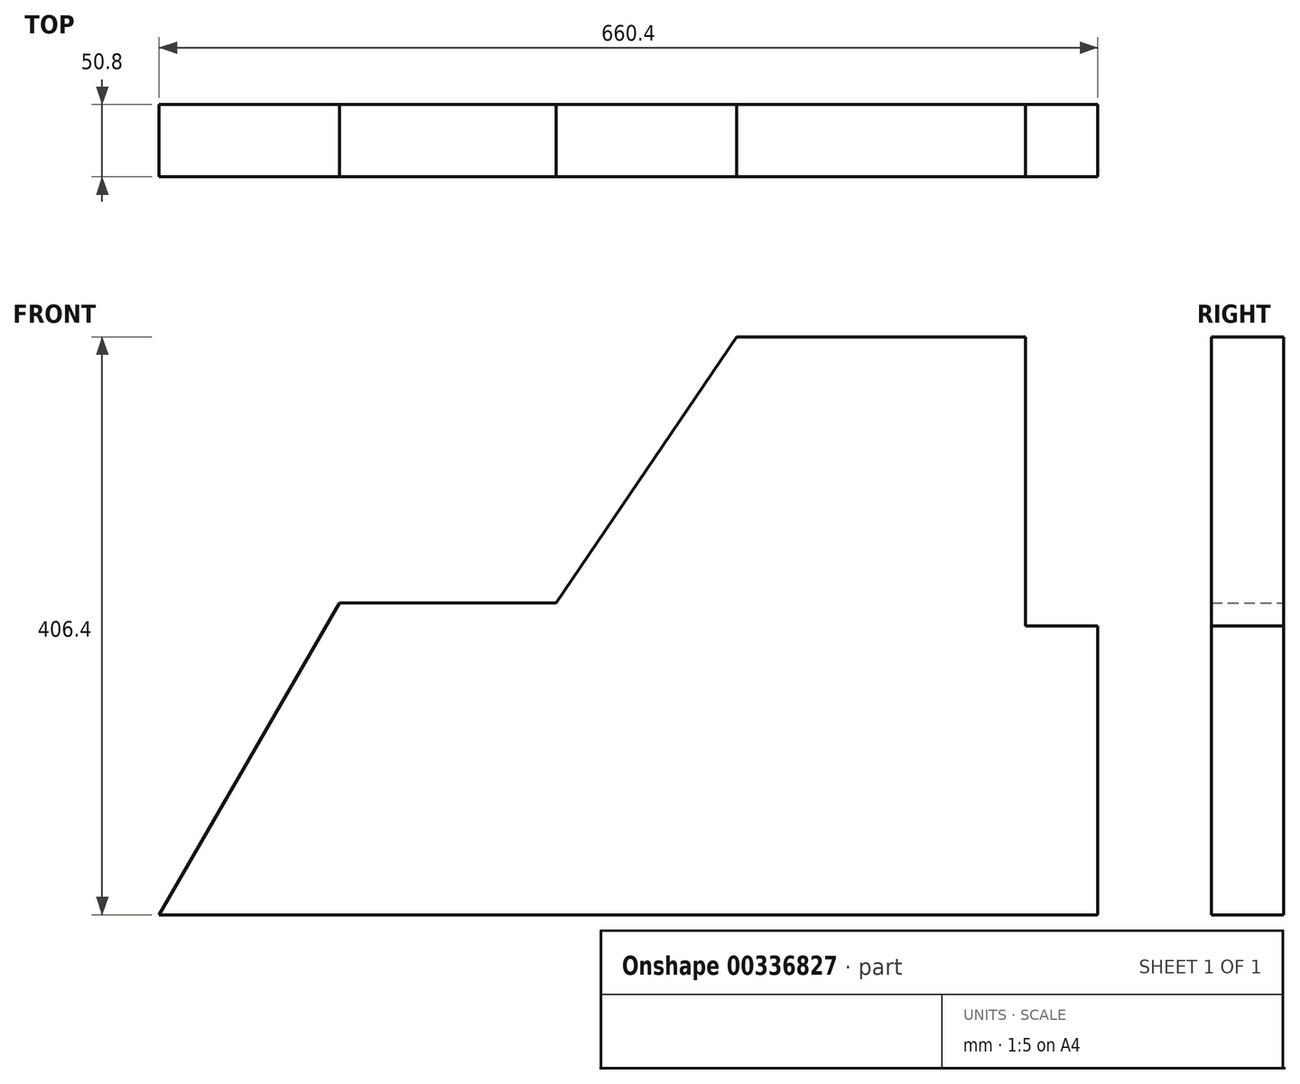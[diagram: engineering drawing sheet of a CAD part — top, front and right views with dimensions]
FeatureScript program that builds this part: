
annotation { "Feature Type Name" : "Feature", "Feature Type Description" : "" }
export const myFeature = defineFeature(function(context is Context, id is Id, definition is map)
    precondition{}
    {
        {
            var Q0;
            Q0=qCreatedBy(makeId("Front.planeOp"),FACE);
            var sketch = newSketch(context, id + "F0", { "sketchPlane" : qUnion([Q0])});
            skLineSegment(sketch, "E0", {"start": v(0, 0) * mm, "end": v(660.4, 0) * mm});
            skLineSegment(sketch, "E1", {"start": v(660.4, 0) * mm, "end": v(660.4, 203.2) * mm});
            skLineSegment(sketch, "E2", {"start": v(660.4, 203.2) * mm, "end": v(609.6, 203.2) * mm});
            skLineSegment(sketch, "E3", {"start": v(609.6, 203.2) * mm, "end": v(609.6, 406.4) * mm});
            skLineSegment(sketch, "E4", {"start": v(609.6, 406.4) * mm, "end": v(406.4, 406.4) * mm});
            skLineSegment(sketch, "E5", {"start": v(406.4, 406.4) * mm, "end": v(279.4, 219.11) * mm});
            skLineSegment(sketch, "E6", {"start": v(279.4, 219.11) * mm, "end": v(127, 219.11) * mm});
            skLineSegment(sketch, "E7", {"start": v(127, 219.11) * mm, "end": v(0, 0) * mm});
            skSolve(sketch);
        }
        {
            var Q0;
            Q0=makeQuery(id+"F0.imprint","IMPRINT",FACE,{"disambiguationData":[TD([[makeQuery(id+"F0.imprint","IMPRINT",EDGE,{"derivedFrom":sQuery(id+"F0.wireOp",EDGE,"E0")}),1.0]])]});
            extrude(context, id + "F1", {"entities" : qUnion([Q0]), "depth" : 50.8 * mm});
        }
    });
